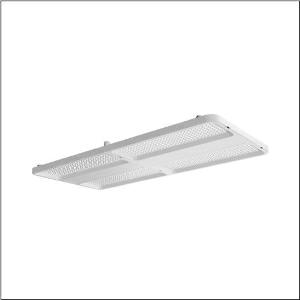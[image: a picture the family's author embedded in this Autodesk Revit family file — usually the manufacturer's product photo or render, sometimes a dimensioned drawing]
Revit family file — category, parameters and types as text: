
# Revit family: highbay_21_maxi_52hn12db4mda02
name_source: partatom
category: Lighting Fixtures
units: mm (PartAtom-declared; Revit-internal decimal feet)

## family parameters
Cut with Voids When Loaded = No
Host = Face
Light Source = No
Part Type = Normal
Room Calculation Point = No
Round Connector Dimension = Use Diameter
Shared = No

## types (1)
- --- (1 x LED, 28000 lm, 144.5 W, 4000K)
    Apparent Load = 144 VA
    CIE Flux Codes = 90 98 100 100 100
    Color Rendering = 80
    Color Temperature = 4000K
    Default Elevation = 1800 mm
    Description = high bay luminaire Highbay 21 maxi; direct symmetric wide distribution, light control with lens of PMMA; UGR ≤ 22 (X = 4H | Y = 8H | S = 0.25H | reflection values 70/50/20); luminous flux: 28.000lm; light colour: 840, colour temperature: 4000K, MacAdam ≤ 3 SDCM (initial), colour rendering: CRI > 80; luminous efficacy: 193,8lm/W; rated service life: 75.000h (L80) at AT= ta max; control: Bluetooth Mesh; for wireless networking: Node luminaire for setting up a local control solution without a higher-level application controller, intelligence completely in the luminaire; no control line such as DALI between the Node multi-sensor luminaires and Nodes is required, wireless integration of other Node luminaires and Node multi-sensor luminaires into the network is possible; number of Node luminaires in the project can be expanded as required, network sizes > 300 Nodes can be realized; can also be connected to lighting or building automation via various gateways upon request; integrated DALI2 ECG provides luminaire data (according to IEC62386, Part 251), energy data (Part 252), and monitoring and analytics data (Part 253) to higher-level systems for further processing; luminaire connection: terminal, 5-pole, max. 2.5mm² (cable entry for one cable, Ø 8.5..16mm); mains connection: 230..240V, AC 50/60Hz; connected load: 144,5W; protection rating (complete): IP66; insulation class (complete): insulation class I (protective earthing); protection symbol: D; impact resistance: IK08; certification: CE, UKCA; internal wiring halogen-free; luminaire LABS conformity tested according to VDMA 24364:2018-05; Suitable for use in the food industry according to the specifications of IFS-Food, HACCP and/or BRC; housing frame of high-performance plastic PA6, matt traffic white (RAL 9016); cover of PMMA; dimension (LxWxH): 946 x 442 x 72mm; permissible operating ambient temperature: -20..+45°C (reducing of maximum allowable ambient temperature of 5°C with ceiling mounting); packaging unit: 1 piece; (delivery without accessories; please order mounting accessories separately)
    Height = 72 mm  [stored 0.23622 ft]
    Lamp = 1 x LED
    Lamp Light Flux = 28000 lm
    Lamp Power = 144.5 W
    Lamp count = 1
    Length = 946 mm
    Luminous efficacy = 194 lm/W
    Manufacturer = Siteco
    ModVariant = No
    Model = 52HN12DB4MDA02
    Mounting Place = Ceiling
    Mounting Type = Pendant
    Number of Poles = 1
    OnlyDefault = Yes
    Power Factor = 1
    Product Name = Highbay 21 maxi
    Product group = high bay luminaire
    ProductGroupID = 902
    Protection Class = Protection class I
    Protection Degree = IP 66
    RLX_Detail_Level = 1
    RLX_Emergency_Light_Flux = 0 lm
    RLX_Emergency_Type = 0
    RLX_Emergency_Type_DB = No
    RlxData = <blob elided: 128473 chars, md5=1f78736d>
    Socket = socket
    Standby Power = 0 W
    System Light Flux = 28000 lm
    System Power = 144 W
    Type Comments = factory setting: luminous flux: 100 % | dim-lin: 254 | 668 mA
    Type Image = l_1363244.jpg
    URL = http://relux.com
    VarID = @adj_014045
    Voltage = 0 V
    Weight = 0.00 kg
    Width = 442 mm

note: [stored X ft] marks values corroborated as IEEE doubles in the binary element streams (Revit-internal decimal feet)

## geometry (parser evidence)
native form markers: Blend x4, Sweep x11
no freeform markers — native parametric forms only
